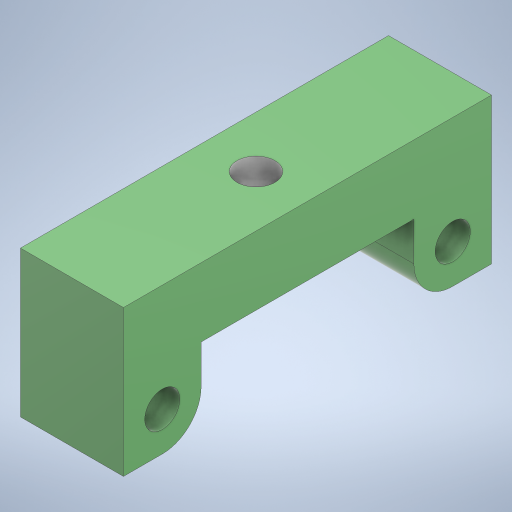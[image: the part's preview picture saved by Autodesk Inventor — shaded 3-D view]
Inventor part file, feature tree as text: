
AUTODESK INVENTOR PART (.ipt)
format: ipt  version: 2023.2 (Build 272271030, 271C)  size: 246,272 bytes
history: native  units: mm
features: extrude x3, sketch x2, plane x1, projected_geometry x1
ambient origin geometry x8: Origin, YZ Plane, XZ Plane, XY Plane, X Axis, Y Axis, Z Axis, Center Point
bodies: Body1 (feature_tree)
feature tree (7):
  extrude  "Extrusion2"  Depth=5.65mm
  plane  "Work Plane1"
  sketch  "Sketch4"  dims[d23=10.0mm d24=10.0mm d25=11.3mm d26=5.1mm d27=15.0mm d28=0.0mm d29=5.5mm d30=5.5mm d31=8.1mm d32=0.0mm d33=0.0mm d34=3.1mm d35=0.0mm d3=0.5mm d4=0.872665mm d5=0.5mm d6=0.872665mm]
  extrude  "Extrusion3"  Depth=10.0mm
  extrude  "Extrusion4"  Depth=11.3mm
  sketch  "Sketch3"  dims[d19=11.3mm d20=5.65mm d22=21.15mm]
  projected_geometry  "Projected Loop1"
